# Revit family: Plastic_Lockers-Salsbury_Industries-95000_Series-1_Wide_Units
name_source: partatom
category: Specialty Equipment
revit_build: Autodesk Revit 2016 (Build: 20150714_1515(x64)
units: mm (PartAtom-declared; Revit-internal decimal feet)

## family parameters
Always vertical = Yes
Cut with Voids When Loaded = No
OmniClass Number = 23.40.00.00
OmniClass Title = Equipment and Furnishings
Part Type = Normal
Room Calculation Point = No
Round Connector Dimension = Use Diameter
Shared = No
Work Plane-Based = No

## types (1)
- 95168
    Assembly Code = C1030310
    Depth = 17.625 "
    Description = 1 Wide - 6 feet high - 18" Deep
    Hasp Material = Steel -Salsbury Finish - Polished Steel
    Height = 73.188 "
    Leg Material = Steel -Salsbury Finish - Polished Steel
    Locker Body Material = ABS Plastic - Salsbury Finish - Dark Gray
    Manufacturer = Salsbury Industries
    MasterFormat Code = 10 51 26
    MasterFormat Title = Plastic Lockers
    Model = 95168
    OmniClass 23 Number = 23.40.00.00
    OmniClass 23 Title = Equipment and Furnishings
    Type Comments = 12" Wide Plastic Locker - Five Tier
    URL = www.lockers.com
    Version = 1.0 (04/30/19)
    Width = 12.563 "

## geometry (parser evidence)
native form markers: Sweep x8
no freeform markers — native parametric forms only
